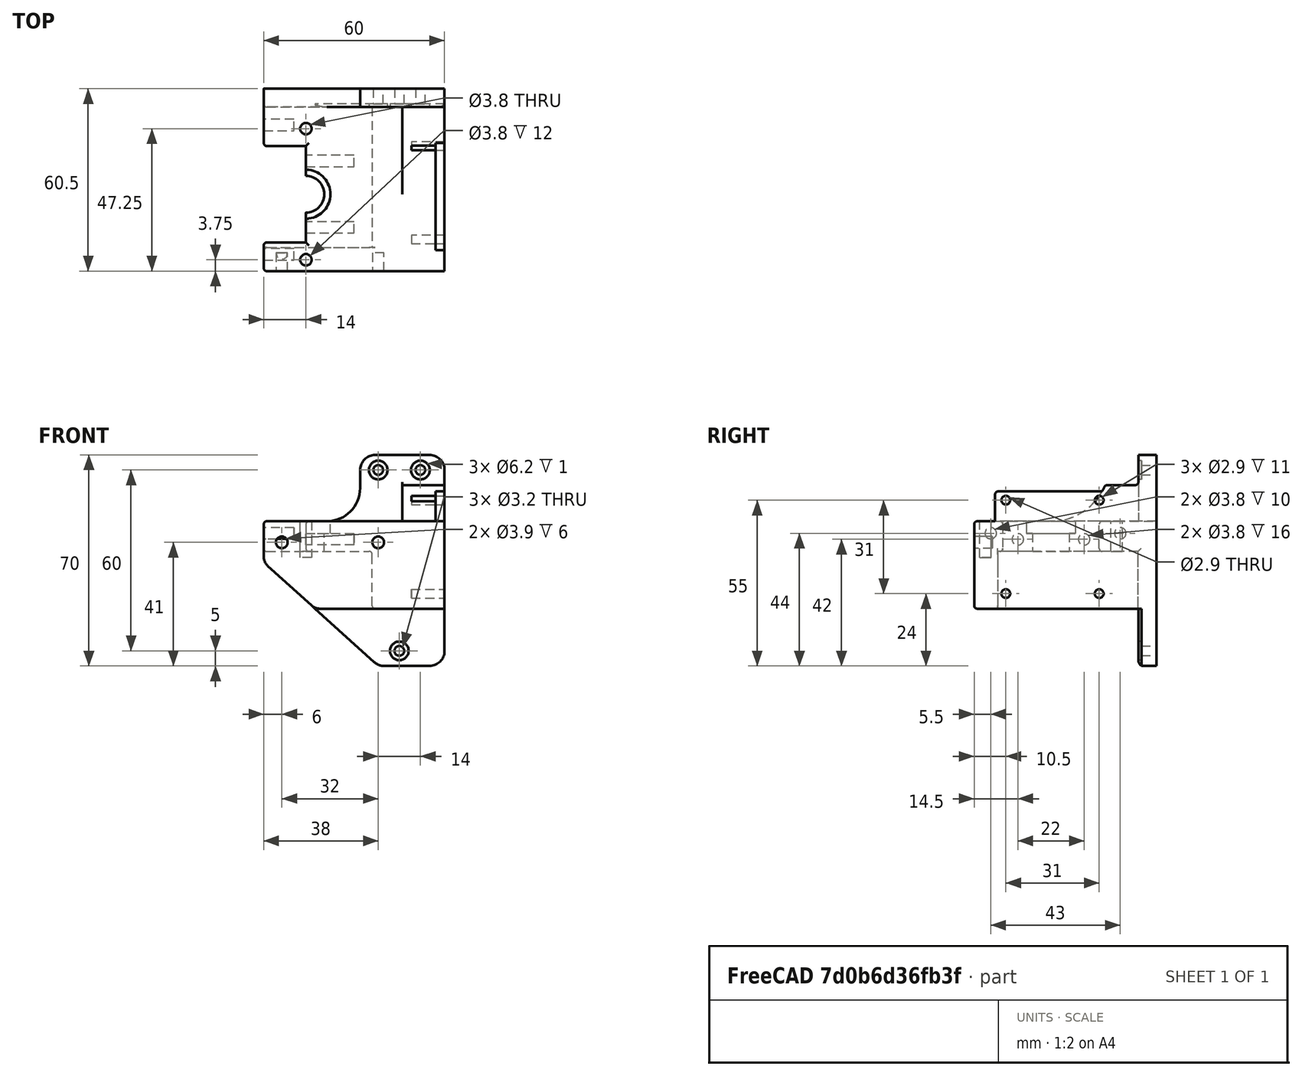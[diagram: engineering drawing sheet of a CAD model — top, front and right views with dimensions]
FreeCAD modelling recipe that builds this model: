
FCSTD DOCUMENT  (FreeCAD 0.19R)
Label: head9.4
License: All rights reserved
LicenseURL: http://en.wikipedia.org/wiki/All_rights_reserved
objects: PartDesign::Fillet×19, Sketcher::SketchObject×18, PartDesign::Pocket×16, PartDesign::Pad×2, PartDesign::Chamfer×1, PartDesign::Body×1, Mesh::Feature×1
note: 95 computed .brp shape members not serialized (recipe doc carries the construction recipe); baked Part::Feature solids carry a one-line shape summary decoded from their .brp

FEATURE [Sketcher::SketchObject] Sketch
  FullyConstrained = true
  MapMode = 5
  Support = -> [XY_Plane]
  sketch-geometry (5):
    g0: LineSegment StartX=0 StartY=0 StartZ=0 EndX=46 EndY=0 EndZ=0
    g1: LineSegment StartX=-14 StartY=0 StartZ=0 EndX=0 EndY=0 EndZ=0
    g2: LineSegment StartX=-14 StartY=0 StartZ=0 EndX=-14 EndY=-60.5 EndZ=0
    g3: LineSegment StartX=-14 StartY=-60.5 StartZ=0 EndX=46 EndY=-60.5 EndZ=0
    g4: LineSegment StartX=46 StartY=-60.5 StartZ=0 EndX=46 EndY=0 EndZ=0
  constraints (14):
    c: Coincident(g-1,g0)
    c: PointOnObject(g0,g-1)
    c: PointOnObject(g1,g-1)
    c: Coincident(g1,g0)
    c: Coincident(g1,g2)
    c: Vertical(g2)
    c: Coincident(g2,g3)
    c: Horizontal(g3)
    c: Coincident(g3,g4)
    c: Coincident(g4,g0)
    c: Vertical(g4)
    c: Distance(g4) = 60.5
    c: DistanceX(g0) = 46
    c: DistanceX(g1) = -14
FEATURE [PartDesign::Pad] Pad
  Direction = (1,1,1)
  Length = 70
  Length2 = 100
  Profile = -> Sketch
  Type = 0
FEATURE [Sketcher::SketchObject] Sketch002  label="platformnotch"
  FullyConstrained = false
  MapMode = 5
  Placement = pos=(0,0,70) rot=(0,0,1;0rad)
  Support = -> [Pad]
  sketch-geometry (6):
    g0: LineSegment StartX=32 StartY=-6 StartZ=0 EndX=32 EndY=-65.096 EndZ=0
    g1: LineSegment StartX=32 StartY=-65.096 StartZ=0 EndX=-40.7834 EndY=-65.096 EndZ=0
    g2: LineSegment StartX=-40.7834 StartY=-65.096 StartZ=0 EndX=-40.7834 EndY=12.9948 EndZ=0
    g3: LineSegment StartX=-40.7834 StartY=12.9948 StartZ=0 EndX=18 EndY=12.9948 EndZ=0
    g4: LineSegment StartX=18 StartY=12.9948 StartZ=0 EndX=18 EndY=-6 EndZ=0
    g5: LineSegment StartX=18 StartY=-6 StartZ=0 EndX=32 EndY=-6 EndZ=0
  constraints (15):
    c: Coincident(g0,g1)
    c: Coincident(g1,g2)
    c: Horizontal(g1)
    c: Vertical(g0)
    c: Vertical(g2)
    c: DistanceX(g0) = 32
    c: DistanceY(g0) = -6
    c: Coincident(g2,g3)
    c: Horizontal(g3)
    c: Coincident(g3,g4)
    c: Coincident(g4,g5)
    c: Coincident(g5,g0)
    c: Horizontal(g5)
    c: Vertical(g4)
    c: DistanceX(g3) = 18
FEATURE [PartDesign::Pocket] Pocket
  BaseFeature = -> Pad
  Length = 22
  Length2 = 100
  Profile = -> Sketch002
  Type = 0
FEATURE [Sketcher::SketchObject] Sketch008  label="pcbnotches"
  FullyConstrained = false
  MapMode = 5
  Placement = pos=(46,0,0) rot=(0.57735,0.57735,0.57735;2.0944rad)
  Support = -> [Pocket]
  sketch-geometry (8):
    g0: LineSegment StartX=-67.659 StartY=19 StartZ=0 EndX=-6 EndY=19 EndZ=0
    g1: LineSegment StartX=-6 StartY=19 StartZ=0 EndX=-6 EndY=-22.4626 EndZ=0
    g2: LineSegment StartX=-6 StartY=-22.4626 StartZ=0 EndX=-67.659 EndY=-22.4626 EndZ=0
    g3: LineSegment StartX=-67.659 StartY=-22.4626 StartZ=0 EndX=-67.659 EndY=19 EndZ=0
    g4: LineSegment StartX=-66.332 StartY=73.6841 StartZ=0 EndX=-6 EndY=73.6841 EndZ=0
    g5: LineSegment StartX=-6 StartY=73.6841 StartZ=0 EndX=-6 EndY=60 EndZ=0
    g6: LineSegment StartX=-6 StartY=60 StartZ=0 EndX=-66.332 EndY=60 EndZ=0
    g7: LineSegment StartX=-66.332 StartY=60 StartZ=0 EndX=-66.332 EndY=73.6841 EndZ=0
  constraints (20):
    c: Coincident(g0,g1)
    c: Coincident(g1,g2)
    c: Coincident(g2,g3)
    c: Coincident(g3,g0)
    c: Horizontal(g0)
    c: Horizontal(g2)
    c: Vertical(g1)
    c: Vertical(g3)
    c: DistanceY(g0) = 19
    c: Coincident(g4,g5)
    c: Coincident(g5,g6)
    c: Coincident(g6,g7)
    c: Coincident(g7,g4)
    c: Horizontal(g4)
    c: Horizontal(g6)
    c: Vertical(g5)
    c: Vertical(g7)
    c: DistanceX(g4) = -6
    c: DistanceY(g5) = 60
    c: DistanceX(g0) = -6
FEATURE [PartDesign::Pocket] Pocket001
  BaseFeature = -> Pocket
  Length = 76
  Length2 = 100
  Profile = -> Sketch008
  Type = 0
FEATURE [Sketcher::SketchObject] Sketch003  label="extredureholes"
  FullyConstrained = true
  MapMode = 5
  Placement = pos=(0,0,48) rot=(0,0,1;0rad)
  Support = -> [Pocket001]
  sketch-geometry (3):
    g0: Circle CenterX=0 CenterY=-13.25 CenterZ=0 NormalX=0 NormalY=0 NormalZ=1 AngleXU=0 Radius=1.9
    g1: Circle CenterX=0 CenterY=-56.75 CenterZ=0 NormalX=0 NormalY=0 NormalZ=1 AngleXU=0 Radius=1.9
    g2: LineSegment StartX=-14.87 StartY=-35 StartZ=0 EndX=14.87 EndY=-35 EndZ=0
  constraints (8):
    c: Distance(g1,g0) = 43.5
    c: Diameter(g1) = 3.8
    c: PointOnObject(g0,g-2)
    c: Symmetric(g2,g2,g-2)
    c: Distance(g2) = 29.74
    c: Symmetric(g1,g0,g2)
    c: DistanceY(g2) = -35
    c: Diameter(g0) = 3.8
FEATURE [PartDesign::Pocket] Pocket002
  BaseFeature = -> Pocket001
  Length = 12
  Length2 = 100
  Profile = -> Sketch003
  Type = 0
FEATURE [Sketcher::SketchObject] Sketch004  label="topNotch"
  FullyConstrained = true
  MapMode = 5
  Placement = pos=(0,0,48) rot=(0,0,1;0rad)
  Support = -> [Pocket002]
  sketch-geometry (4):
    g0: ArcOfCircle CenterX=0 CenterY=-35 CenterZ=0 NormalX=0 NormalY=0 NormalZ=1 AngleXU=0 Radius=8.125 StartAngle=4.71239 EndAngle=7.85398
    g1: LineSegment StartX=-1.5e-15 StartY=-43.125 StartZ=0 EndX=-25 EndY=-43.125 EndZ=0
    g2: LineSegment StartX=-25 StartY=-43.125 StartZ=0 EndX=-25 EndY=-26.875 EndZ=0
    g3: LineSegment StartX=-25 StartY=-26.875 StartZ=0 EndX=-2.629e-13 EndY=-26.875 EndZ=0
  constraints (11):
    c: PointOnObject(g0,g-2)
    c: Diameter(g0) = 16.25
    c: DistanceY(g0) = -35
    c: Coincident(g1,g2)
    c: Coincident(g2,g3)
    c: Distance(g3) = 25
    c: Tangent(g3,g0) = 1.5708
    c: Tangent(g1,g0) = 1.5708
    c: Horizontal(g3)
    c: Horizontal(g1)
    c: Vertical(g2)
FEATURE [PartDesign::Pocket] Pocket003
  BaseFeature = -> Pocket002
  Length = 4
  Length2 = 100
  Profile = -> Sketch004
  Type = 0
FEATURE [Sketcher::SketchObject] Sketch018  label="innergroove"
  FullyConstrained = true
  MapMode = 5
  Placement = pos=(0,0,44) rot=(0,0,1;0rad)
  Support = -> [Pocket003]
  sketch-geometry (4):
    g0: ArcOfCircle CenterX=0 CenterY=-35 CenterZ=0 NormalX=0 NormalY=0 NormalZ=1 AngleXU=0 Radius=6.1 StartAngle=4.71239 EndAngle=7.85398
    g1: LineSegment StartX=-1.1e-15 StartY=-41.1 StartZ=0 EndX=-50 EndY=-41.1 EndZ=0
    g2: LineSegment StartX=1.9e-15 StartY=-28.9 StartZ=0 EndX=-50 EndY=-28.9 EndZ=0
    g3: LineSegment StartX=-50 StartY=-41.1 StartZ=0 EndX=-50 EndY=-28.9 EndZ=0
  constraints (11):
    c: PointOnObject(g0,g-2)
    c: Coincident(g3,g1)
    c: Coincident(g3,g2)
    c: Tangent(g1,g0) = 1.5708
    c: Tangent(g2,g0) = -1.5708
    c: DistanceY(g0) = -35
    c: Diameter(g0) = 12.2
    c: Distance(g1) = 50
    c: Vertical(g3)
    c: Horizontal(g1)
    c: Horizontal(g2)
FEATURE [PartDesign::Pocket] Pocket004
  BaseFeature = -> Pocket003
  Length = 6
  Length2 = 100
  Profile = -> Sketch018
  Type = 0
FEATURE [Sketcher::SketchObject] Sketch009  label="PCBholes"
  FullyConstrained = true
  MapMode = 5
  Placement = pos=(46,0,0) rot=(0.57735,0.57735,0.57735;2.0944rad)
  Support = -> [Pocket004]
  sketch-geometry (5):
    g0: Circle CenterX=-50 CenterY=55 CenterZ=0 NormalX=0 NormalY=0 NormalZ=1 AngleXU=0 Radius=1.35
    g1: Circle CenterX=-19 CenterY=24 CenterZ=0 NormalX=0 NormalY=0 NormalZ=1 AngleXU=0 Radius=1.35
    g2: LineSegment StartX=-50 StartY=55 StartZ=0 EndX=-19 EndY=24 EndZ=0
    g3: Circle CenterX=-19 CenterY=55 CenterZ=0 NormalX=0 NormalY=0 NormalZ=1 AngleXU=0 Radius=1.35
    g4: Circle CenterX=-50 CenterY=24 CenterZ=0 NormalX=0 NormalY=0 NormalZ=1 AngleXU=0 Radius=1.35
  constraints (14):
    c: Coincident(g2,g0)
    c: Coincident(g2,g1)
    c: Angle(g2) = -0.785398
    c: DistanceX(g1) = -19
    c: DistanceY(g1) = 24
    c: Diameter(g4) = 2.7
    c: Equal(g4,g0)
    c: Equal(g4,g3)
    c: Equal(g4,g1)
    c: DistanceY(g4,g0) = 31
    c: DistanceX(g0,g3) = 31
    c: DistanceX(g4,g1) = 31
    c: DistanceY(g4) = 24
    c: DistanceY(g1,g3) = 31
FEATURE [PartDesign::Pocket] Pocket005
  BaseFeature = -> Pocket004
  Length = 10
  Length2 = 100
  Profile = -> Sketch009
  Type = 0
FEATURE [Sketcher::SketchObject] Sketch030
  FullyConstrained = false
  MapMode = 5
  Placement = pos=(0,0,48) rot=(0,0,1;0rad)
  Support = -> [Pocket005]
  sketch-geometry (5):
    g0: LineSegment StartX=-28.769 StartY=-19 StartZ=0 EndX=0 EndY=-19 EndZ=0
    g1: LineSegment StartX=0 StartY=-19 StartZ=0 EndX=0 EndY=-51 EndZ=0
    g2: LineSegment StartX=0 StartY=-51 StartZ=0 EndX=-28.769 EndY=-51 EndZ=0
    g3: LineSegment StartX=-28.769 StartY=-51 StartZ=0 EndX=-28.769 EndY=-19 EndZ=0
    g4: LineSegment StartX=-7.77915 StartY=-35 StartZ=0 EndX=15.2351 EndY=-35 EndZ=0
  constraints (12):
    c: Coincident(g0,g1)
    c: Coincident(g1,g2)
    c: Coincident(g2,g3)
    c: Coincident(g3,g0)
    c: Horizontal(g0)
    c: Horizontal(g2)
    c: Vertical(g1)
    c: Vertical(g3)
    c: PointOnObject(g1,g-2)
    c: Distance(g1) = 32
    c: Symmetric(g0,g1,g4)
    c: DistanceY(g4) = -35
FEATURE [PartDesign::Pocket] Pocket006
  BaseFeature = -> Pocket005
  Length = 5
  Length2 = 100
  Profile = -> Sketch030
  Type = 1
FEATURE [Sketcher::SketchObject] Sketch031
  FullyConstrained = false
  MapMode = 5
  Placement = pos=(-14,0,0) rot=(0.57735,-0.57735,-0.57735;2.0944rad)
  Support = -> [Pocket006]
  sketch-geometry (4):
    g0: LineSegment StartX=6.1 StartY=38 StartZ=0 EndX=52.7193 EndY=38 EndZ=0
    g1: LineSegment StartX=52.7193 StartY=38 StartZ=0 EndX=52.7193 EndY=2.95128 EndZ=0
    g2: LineSegment StartX=52.7193 StartY=2.95128 StartZ=0 EndX=6.1 EndY=2.95128 EndZ=0
    g3: LineSegment StartX=6.1 StartY=2.95128 StartZ=0 EndX=6.1 EndY=38 EndZ=0
  constraints (10):
    c: Coincident(g0,g1)
    c: Coincident(g1,g2)
    c: Coincident(g2,g3)
    c: Coincident(g3,g0)
    c: Horizontal(g0)
    c: Horizontal(g2)
    c: Vertical(g1)
    c: Vertical(g3)
    c: DistanceX(g0) = 6.1
    c: DistanceY(g0) = 38
FEATURE [PartDesign::Pocket] Pocket007
  BaseFeature = -> Pocket006
  Length = 36
  Length2 = 100
  Profile = -> Sketch031
  Type = 0
FEATURE [Sketcher::SketchObject] Sketch032  label="FanScrews"
  ExternalGeometry = -> [Pocket007]
  FullyConstrained = true
  MapMode = 5
  Placement = pos=(-14,0,0) rot=(0.57735,-0.57735,-0.57735;2.0944rad)
  Support = -> [Pocket007]
  sketch-geometry (2):
    g0: Circle CenterX=12 CenterY=44 CenterZ=0 NormalX=0 NormalY=0 NormalZ=1 AngleXU=0 Radius=1.9
    g1: Circle CenterX=55 CenterY=44 CenterZ=0 NormalX=0 NormalY=0 NormalZ=1 AngleXU=0 Radius=1.9
  constraints (6):
    c: Diameter(g0) = 3.8
    c: DistanceX(g0) = 12
    c: DistanceY(g0) = 44
    c: Diameter(g1) = 3.8
    c: DistanceY(g1) = 44
    c: DistanceX(g1) = 55
FEATURE [PartDesign::Pocket] Pocket008
  BaseFeature = -> Pocket007
  Length = 10
  Length2 = 100
  Profile = -> Sketch032
  Type = 0
FEATURE [Sketcher::SketchObject] Sketch013  label="groovescrews"
  FullyConstrained = false
  MapMode = 5
  Placement = pos=(0,0,0) rot=(0.57735,-0.57735,-0.57735;2.0944rad)
  Support = -> [Pocket008]
  sketch-geometry (3):
    g0: Circle CenterX=24 CenterY=42 CenterZ=0 NormalX=0 NormalY=0 NormalZ=1 AngleXU=0 Radius=1.9
    g1: Circle CenterX=46 CenterY=42 CenterZ=0 NormalX=0 NormalY=0 NormalZ=1 AngleXU=0 Radius=1.9
    g2: LineSegment StartX=35 StartY=87.2769 StartZ=0 EndX=35 EndY=69.6255 EndZ=0
  constraints (6):
    c: Distance(g1,g0) = 22
    c: Diameter(g1) = 3.8
    c: Equal(g1,g0)
    c: Vertical(g2)
    c: Symmetric(g1,g0,g2)
    c: DistanceX(g2) = 35
FEATURE [PartDesign::Pocket] Pocket009
  BaseFeature = -> Pocket008
  Length = 16
  Length2 = 100
  Profile = -> Sketch013
  Type = 0
FEATURE [Sketcher::SketchObject] Sketch010  label="mountholes"
  FullyConstrained = true
  MapMode = 5
  Placement = pos=(0,0,0) rot=(0,0.707107,0.707107;3.14159rad)
  Support = -> [Pocket009]
  sketch-geometry (3):
    g0: Circle CenterX=-31 CenterY=5 CenterZ=0 NormalX=0 NormalY=0 NormalZ=1 AngleXU=0 Radius=1.6
    g1: Circle CenterX=-38 CenterY=65 CenterZ=0 NormalX=0 NormalY=0 NormalZ=1 AngleXU=0 Radius=1.6
    g2: Circle CenterX=-24 CenterY=65 CenterZ=0 NormalX=0 NormalY=0 NormalZ=1 AngleXU=0 Radius=1.6
  constraints (9):
    c: Diameter(g0) = 3.2
    c: Equal(g0,g2)
    c: Equal(g0,g1)
    c: DistanceX(g0) = -31
    c: Distance(g1,g2) = 14
    c: DistanceX(g2) = -24
    c: DistanceY(g0) = 5
    c: DistanceY(g2) = 65
    c: DistanceY(g1) = 65
FEATURE [PartDesign::Pocket] Pocket010
  BaseFeature = -> Pocket009
  Length = 7
  Length2 = 100
  Profile = -> Sketch010
  Type = 0
FEATURE [Sketcher::SketchObject] Sketch033  label="ANgler"
  FullyConstrained = false
  MapMode = 5
  Placement = pos=(0,0,0) rot=(0,0.707107,0.707107;3.14159rad)
  Support = -> [Pocket010]
  sketch-geometry (3):
    g0: LineSegment StartX=21.9958 StartY=41.6537 StartZ=0 EndX=-34.9081 EndY=-9.83073 EndZ=0
    g1: LineSegment StartX=21.9958 StartY=41.6537 StartZ=0 EndX=21.9958 EndY=-12.4114 EndZ=0
    g2: LineSegment StartX=21.9958 StartY=-12.4114 StartZ=0 EndX=-34.9081 EndY=-9.83073 EndZ=0
  constraints (4):
    c: Coincident(g0,g1)
    c: Vertical(g1)
    c: Coincident(g1,g2)
    c: Coincident(g2,g0)
FEATURE [PartDesign::Pocket] Pocket011
  BaseFeature = -> Pocket010
  Length = 5
  Length2 = 100
  Profile = -> Sketch033
  Type = 1
FEATURE [Sketcher::SketchObject] Sketch034
  ExternalGeometry = -> [Pocket011]
  FullyConstrained = true
  MapMode = 5
  Placement = pos=(32,0,0) rot=(0.57735,-0.57735,-0.57735;2.0944rad)
  Support = -> [Pocket011]
  sketch-geometry (4):
    g0: ArcOfCircle CenterX=35 CenterY=67.5 CenterZ=0 NormalX=0 NormalY=0 NormalZ=1 AngleXU=0 Radius=19.5 StartAngle=3.14159 EndAngle=4.71239
    g1: LineSegment StartX=35 StartY=48 StartZ=0 EndX=74.47 EndY=48 EndZ=0
    g2: LineSegment StartX=15.5 StartY=67.5 StartZ=0 EndX=74.47 EndY=67.5 EndZ=0
    g3: LineSegment StartX=74.47 StartY=67.5 StartZ=0 EndX=74.47 EndY=48 EndZ=0
  constraints (13):
    c: DistanceX(g0) = 35
    c: Diameter(g0) = 39
    c: Coincident(g1,g0)
    c: Horizontal(g1)
    c: Coincident(g0,g2)
    c: Coincident(g2,g3)
    c: Coincident(g3,g1)
    c: Horizontal(g2)
    c: Perpendicular(g0,g2)
    c: PointOnObject(g-3,g1)
    c: Vertical(g3)
    c: Distance(g2) = 58.97
    c: DistanceX(g0) = 35
FEATURE [PartDesign::Pocket] Pocket012
  BaseFeature = -> Pocket011
  Length = 10
  Length2 = 100
  Profile = -> Sketch034
  Type = 1
FEATURE [Sketcher::SketchObject] Sketch035  label="FrontMountHoles"
  ExternalGeometry = -> [Pocket012]
  FullyConstrained = false
  MapMode = 5
  Placement = pos=(0,-60.5,0) rot=(1,0,0;1.5708rad)
  Support = -> [Pocket012]
  sketch-geometry (3):
    g0: Circle CenterX=-8 CenterY=41 CenterZ=0 NormalX=0 NormalY=0 NormalZ=1 AngleXU=0 Radius=1.95
    g1: Circle CenterX=24 CenterY=41 CenterZ=0 NormalX=0 NormalY=0 NormalZ=1 AngleXU=0 Radius=1.95
    g2: LineSegment StartX=-4.95622 StartY=-23 StartZ=0 EndX=5.01253 EndY=-23 EndZ=0
  constraints (8):
    c: Diameter(g1) = 3.9
    c: Equal(g1,g0)
    c: DistanceX(g0,g-1) = 8
    c: Distance(g1,g0) = 32
    c: Horizontal(g2)
    c: Distance(g2,g-3) = 71
    c: Distance(g1,g2) = 64
    c: Distance(g0,g2) = 64
FEATURE [PartDesign::Pocket] Pocket013
  BaseFeature = -> Pocket012
  Length = 6
  Length2 = 100
  Profile = -> Sketch035
  Type = 0
FEATURE [PartDesign::Fillet] Fillet
  Base = -> Pocket013 [Edge32]
  BaseFeature = -> Pocket013
  Radius = 11
  SupportTransform = false
FEATURE [PartDesign::Fillet] Fillet001
  Base = -> Fillet [Edge15,Edge20,Edge38,Edge51]
  BaseFeature = -> Fillet
  Radius = 5
  SupportTransform = false
FEATURE [PartDesign::Fillet] Fillet002
  Base = -> Fillet001 [Edge61]
  BaseFeature = -> Fillet001
  Radius = 4
  SupportTransform = false
FEATURE [PartDesign::Fillet] Fillet003
  Base = -> Fillet002 [Edge124]
  BaseFeature = -> Fillet002
  Radius = 4
  SupportTransform = false
FEATURE [PartDesign::Fillet] Fillet004
  Base = -> Fillet003 [Edge11]
  BaseFeature = -> Fillet003
  Radius = 4
  SupportTransform = false
FEATURE [PartDesign::Fillet] Fillet005
  Base = -> Fillet004 [Edge19]
  BaseFeature = -> Fillet004
  Radius = 1
  SupportTransform = false
FEATURE [PartDesign::Fillet] Fillet006
  Base = -> Fillet005 [Edge57]
  BaseFeature = -> Fillet005
  Radius = 1
  SupportTransform = false
FEATURE [Sketcher::SketchObject] Sketch036
  FullyConstrained = false
  MapMode = 5
  Placement = pos=(46,0,0) rot=(0.57735,0.57735,0.57735;2.0944rad)
  Support = -> [Fillet006]
  sketch-geometry (4):
    g0: LineSegment StartX=-53.5397 StartY=57.9121 StartZ=0 EndX=-16.5185 EndY=57.9121 EndZ=0
    g1: LineSegment StartX=-16.5185 StartY=57.9121 StartZ=0 EndX=-16.5185 EndY=21.9397 EndZ=0
    g2: LineSegment StartX=-16.5185 StartY=21.9397 StartZ=0 EndX=-53.5397 EndY=21.9397 EndZ=0
    g3: LineSegment StartX=-53.5397 StartY=21.9397 StartZ=0 EndX=-53.5397 EndY=57.9121 EndZ=0
  constraints (8):
    c: Coincident(g0,g1)
    c: Coincident(g1,g2)
    c: Coincident(g2,g3)
    c: Coincident(g3,g0)
    c: Horizontal(g0)
    c: Horizontal(g2)
    c: Vertical(g1)
    c: Vertical(g3)
FEATURE [PartDesign::Pad] Pad001
  BaseFeature = -> Fillet006
  Direction = (1,1,1)
  Length = 3
  Length2 = 100
  Profile = -> Sketch036
  Reversed = true
  Type = 0
FEATURE [Sketcher::SketchObject] Sketch037
  ExternalGeometry = -> [Pad001]
  FullyConstrained = true
  MapMode = 5
  Placement = pos=(46,0,0) rot=(0.57735,0.57735,0.57735;2.0944rad)
  Support = -> [Pad001]
  sketch-geometry (4):
    g0: Circle CenterX=-19 CenterY=55 CenterZ=0 NormalX=0 NormalY=0 NormalZ=1 AngleXU=0 Radius=1.45
    g1: Circle CenterX=-19 CenterY=24 CenterZ=0 NormalX=0 NormalY=0 NormalZ=1 AngleXU=0 Radius=1.45
    g2: Circle CenterX=-50 CenterY=24 CenterZ=0 NormalX=0 NormalY=0 NormalZ=1 AngleXU=0 Radius=1.45
    g3: Circle CenterX=-50 CenterY=55 CenterZ=0 NormalX=0 NormalY=0 NormalZ=1 AngleXU=0 Radius=1.45
  constraints (9):
    c: Diameter(g2) = 2.9
    c: Equal(g2,g3)
    c: Equal(g2,g0)
    c: Equal(g2,g1)
    c: Coincident(g-5,g2)
    c: Coincident(g1,g-3)
    c: Coincident(g0,g-4)
    c: Distance(g3,g0) = 31
    c: Distance(g2,g3) = 31
FEATURE [PartDesign::Pocket] Pocket014
  BaseFeature = -> Pad001
  Length = 11
  Length2 = 100
  Profile = -> Sketch037
  Type = 0
FEATURE [PartDesign::Fillet] Fillet007
  Base = -> Pocket014 [Edge91]
  BaseFeature = -> Pocket014
  Radius = 1
  SupportTransform = false
FEATURE [PartDesign::Fillet] Fillet008
  Base = -> Fillet007 [Edge170]
  BaseFeature = -> Fillet007
  Radius = 1
  SupportTransform = false
FEATURE [PartDesign::Fillet] Fillet009
  Base = -> Fillet008 [Edge20]
  BaseFeature = -> Fillet008
  Radius = 1
  SupportTransform = false
FEATURE [PartDesign::Fillet] Fillet010
  Base = -> Fillet009 [Edge63]
  BaseFeature = -> Fillet009
  Radius = 1
  SupportTransform = false
FEATURE [PartDesign::Fillet] Fillet011
  Base = -> Fillet010 [Edge40,Edge123]
  BaseFeature = -> Fillet010
  Radius = 1
  SupportTransform = false
FEATURE [PartDesign::Fillet] Fillet012
  Base = -> Fillet011 [Edge66,Edge12]
  BaseFeature = -> Fillet011
  Radius = 1
  SupportTransform = false
FEATURE [PartDesign::Fillet] Fillet013
  Base = -> Fillet012 [Edge114]
  BaseFeature = -> Fillet012
  Radius = 1
  SupportTransform = false
FEATURE [PartDesign::Fillet] Fillet014
  Base = -> Fillet013 [Edge70]
  BaseFeature = -> Fillet013
  Radius = 1
  SupportTransform = false
FEATURE [PartDesign::Fillet] Fillet015
  Base = -> Fillet014 [Edge5,Edge9]
  BaseFeature = -> Fillet014
  Radius = 1
  SupportTransform = false
FEATURE [PartDesign::Fillet] Fillet016
  Base = -> Fillet015 [Edge94,Edge86]
  BaseFeature = -> Fillet015
  Radius = 1
  SupportTransform = false
FEATURE [PartDesign::Chamfer] Chamfer
  Angle = 45
  Base = -> Fillet016 [Edge233]
  BaseFeature = -> Fillet016
  ChamferType = 0
  FlipDirection = false
  Size = 1
  Size2 = 1
  SupportTransform = false
FEATURE [PartDesign::Fillet] Fillet017
  Base = -> Chamfer [Edge16]
  BaseFeature = -> Chamfer
  Radius = 2
  SupportTransform = false
FEATURE [PartDesign::Fillet] Fillet018
  Base = -> Fillet017 [Edge51]
  BaseFeature = -> Fillet017
  Radius = 1
  SupportTransform = false
FEATURE [Sketcher::SketchObject] Sketch038
  ExternalGeometry = -> [Fillet018]
  FullyConstrained = true
  MapMode = 5
  Placement = pos=(0,-6,0) rot=(1,0,0;1.5708rad)
  Support = -> [Fillet018]
  sketch-geometry (3):
    g0: Circle CenterX=24 CenterY=65 CenterZ=0 NormalX=0 NormalY=0 NormalZ=1 AngleXU=0 Radius=3.1
    g1: Circle CenterX=38 CenterY=65 CenterZ=0 NormalX=0 NormalY=0 NormalZ=1 AngleXU=0 Radius=3.1
    g2: Circle CenterX=31 CenterY=5 CenterZ=0 NormalX=0 NormalY=0 NormalZ=1 AngleXU=0 Radius=3.1
  constraints (6):
    c: Diameter(g1) = 6.2
    c: Equal(g1,g2)
    c: Equal(g1,g0)
    c: Coincident(g0,g-4)
    c: Coincident(g1,g-3)
    c: Coincident(g2,g-5)
FEATURE [PartDesign::Pocket] Pocket015
  BaseFeature = -> Fillet018
  Length = 1
  Length2 = 100
  Profile = -> Sketch038
  Type = 0
FEATURE [PartDesign::Body] Body
  Group = -> [Sketch,Pad,Sketch002,Sketch003,Sketch004,Sketch008,Sketch009,Sketch010,Sketch013,Sketch018,Pocket,Pocket001,Pocket002,Pocket003,Pocket004,Pocket005,Sketch030,Pocket006,Sketch031,Pocket007,Sketch032,Pocket008,Pocket009,Pocket010,Sketch033,Pocket011,Sketch034,Pocket012,Sketch035,Pocket013,Fillet,Fillet001,Fillet002,Fillet003,Fillet004,Fillet005,Fillet006,Sketch036,Pad001,Sketch037,Pocket014,+15 more]
  Origin = -> Origin
  Tip = -> Pocket015
FEATURE [Mesh::Feature] Mesh  label="Pocket015 (Meshed)"
